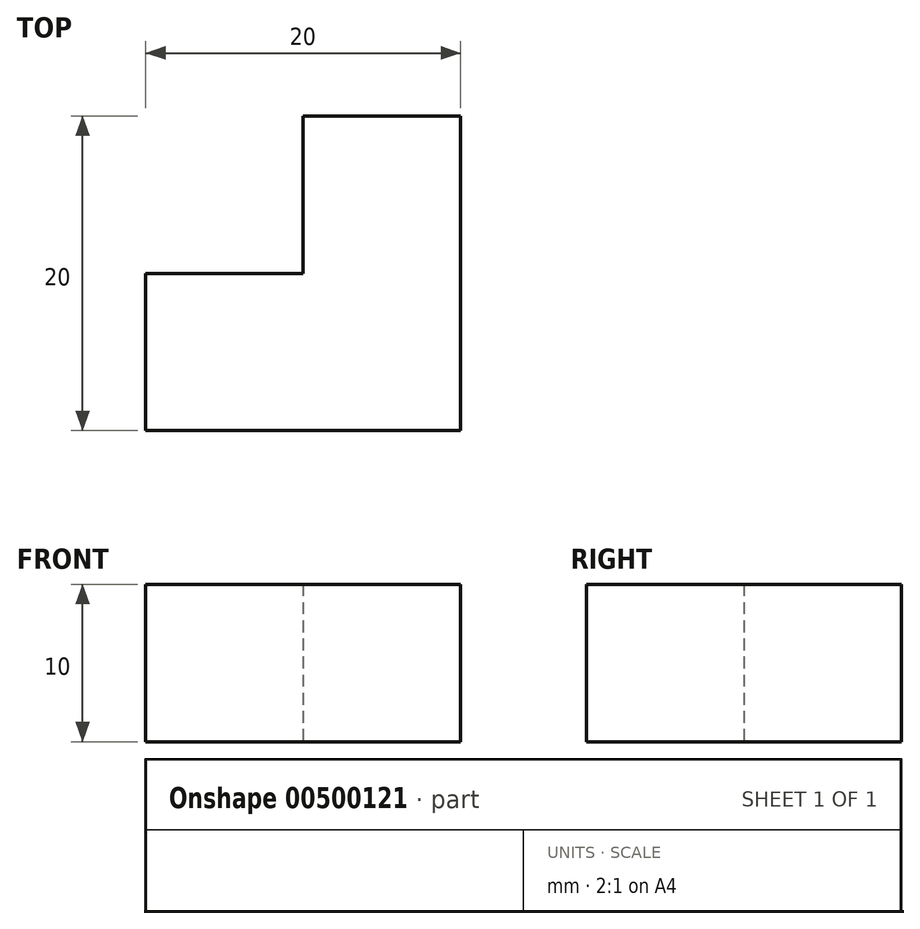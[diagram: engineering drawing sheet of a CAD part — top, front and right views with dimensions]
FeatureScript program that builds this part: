
annotation { "Feature Type Name" : "Feature", "Feature Type Description" : "" }
export const myFeature = defineFeature(function(context is Context, id is Id, definition is map)
    precondition{}
    {
        {
            var Q0;
            Q0=qCreatedBy(makeId("Top.planeOp"),FACE);
            var sketch = newSketch(context, id + "F0", { "sketchPlane" : qUnion([Q0])});
            skLineSegment(sketch, "E0", {"start": v(0, 0) * mm, "end": v(0, 10) * mm});
            skLineSegment(sketch, "E1", {"start": v(0, 10) * mm, "end": v(10, 10) * mm});
            skLineSegment(sketch, "E2", {"start": v(10, 10) * mm, "end": v(10, 20) * mm});
            skLineSegment(sketch, "E3", {"start": v(10, 20) * mm, "end": v(20, 20) * mm});
            skLineSegment(sketch, "E4", {"start": v(20, 20) * mm, "end": v(20, 0) * mm});
            skLineSegment(sketch, "E5", {"start": v(20, 0) * mm, "end": v(0, 0) * mm});
            skSolve(sketch);
        }
        {
            var Q0;
            Q0 = qSketchRegion(id + "F0", true);
            extrude(context, id + "F1", {"entities" : qUnion([Q0]), "depth" : 10 * mm});
        }
    });
